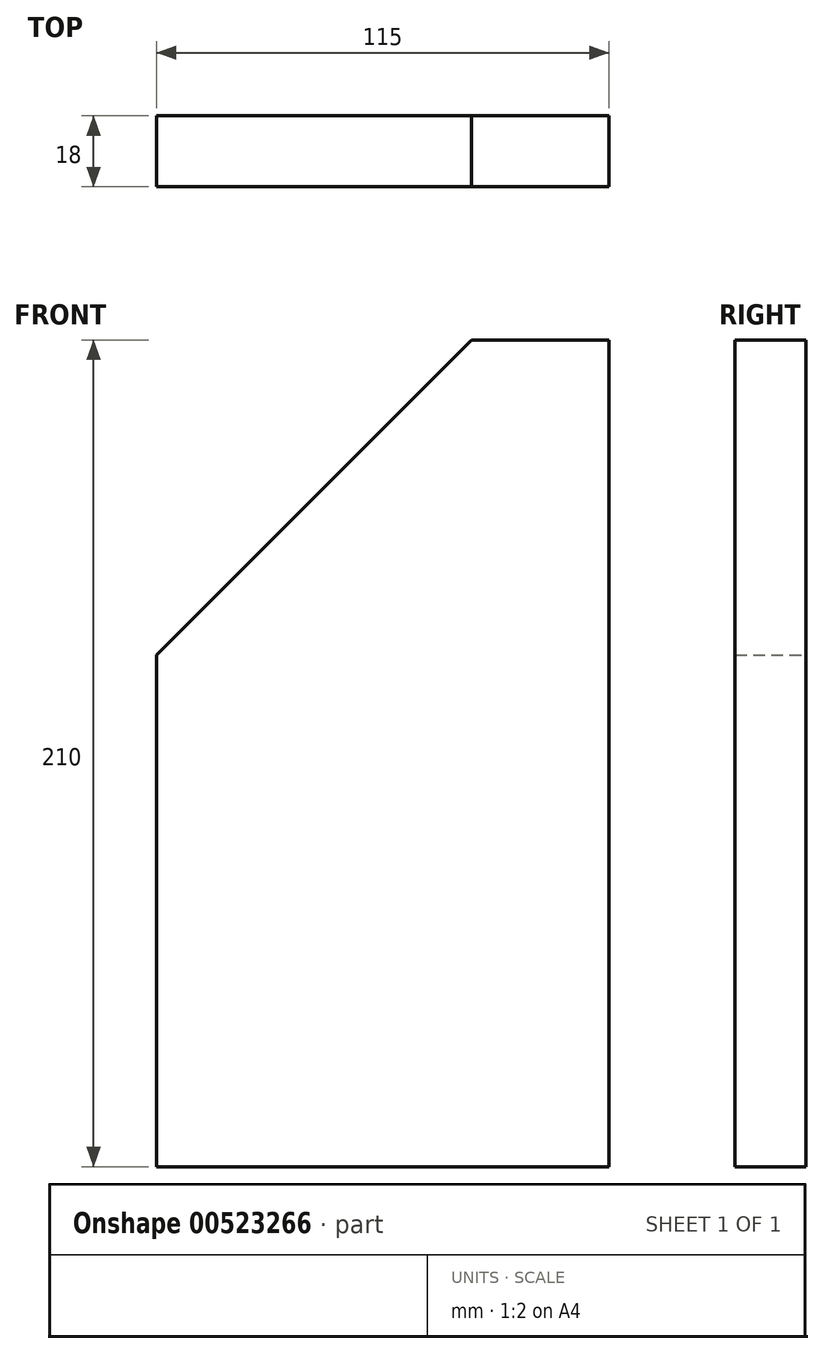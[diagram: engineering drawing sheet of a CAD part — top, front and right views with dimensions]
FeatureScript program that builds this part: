
annotation { "Feature Type Name" : "Feature", "Feature Type Description" : "" }
export const myFeature = defineFeature(function(context is Context, id is Id, definition is map)
    precondition{}
    {
        {
            var Q0;
            Q0=qCreatedBy(makeId("Front.planeOp"),FACE);
            var sketch = newSketch(context, id + "F0", { "sketchPlane" : qUnion([Q0])});
            skLineSegment(sketch, "E0.bottom", {"start": v(0, 0) * mm, "end": v(115, 0) * mm});
            skLineSegment(sketch, "E0.top", {"start": v(0, 210) * mm, "end": v(115, 210) * mm});
            skLineSegment(sketch, "E0.left", {"start": v(0, 0) * mm, "end": v(0, 210) * mm});
            skLineSegment(sketch, "E0.right", {"start": v(115, 0) * mm, "end": v(115, 210) * mm});
            skSolve(sketch);
        }
        {
            var Q0;
            Q0=makeQuery(id+"F0.imprint","IMPRINT",FACE,{"disambiguationData":[TD([[makeQuery(id+"F0.imprint","IMPRINT",EDGE,{"derivedFrom":sQuery(id+"F0.wireOp",EDGE,"E0.bottom")}),1.0]])]});
            extrude(context, id + "F1", {"entities" : qUnion([Q0]), "depth" : 18 * mm, "offsetDistance" : 25 * mm});
        }
        {
            var Q0;
            Q0=makeQuery(id+"F1.opExtrude","SWEPT_EDGE",EDGE,{"disambiguationData":[OSD([sQuery(id+"F0.wireOp",EDGE,"E0.top"),sQuery(id+"F0.wireOp",EDGE,"E0.left")])]});
            chamfer(context, id + "F2", {"entities" : qUnion([Q0]), "width" : 80 * mm, "tangentPropagation" : true});
        }
    });
